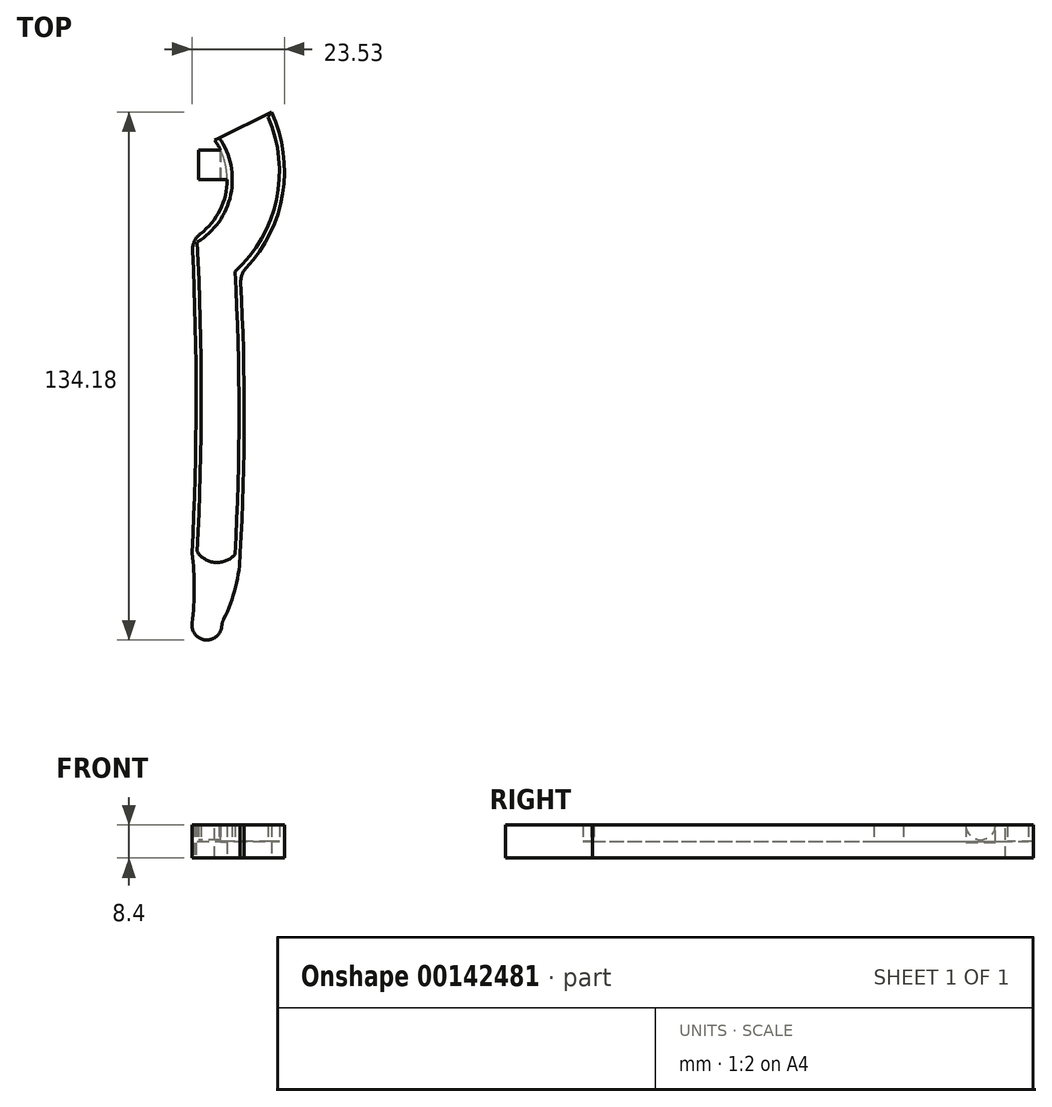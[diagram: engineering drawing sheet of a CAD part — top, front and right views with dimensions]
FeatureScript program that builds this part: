
annotation { "Feature Type Name" : "Feature", "Feature Type Description" : "" }
export const myFeature = defineFeature(function(context is Context, id is Id, definition is map)
    precondition{}
    {
        {
            var Q0;
            Q0=qCreatedBy(makeId("Top.planeOp"),FACE);
            var sketch = newSketch(context, id + "F0", { "sketchPlane" : qUnion([Q0])});
            skArc(sketch, "E0", {"start": v(-18, -31.8) * mm, "mid": v(-9.08, -15.9) * mm, "end": v(-18, 0) * mm});
            skArc(sketch, "E1", {"start": v(-8.38, -39.3) * mm, "mid": v(2.12, -21) * mm, "end": v(0, 0) * mm});
            skArc(sketch, "E2", {"start": v(-18, -110.4) * mm, "mid": v(-17, -71.1) * mm, "end": v(-18, -31.8) * mm});
            skArc(sketch, "E3", {"start": v(-8.38, -111.1) * mm, "mid": v(-7.37, -75.2) * mm, "end": v(-8.38, -39.3) * mm});
            skArc(sketch, "E4", {"start": v(-18, -110.4) * mm, "mid": v(-13.37, -113.18) * mm, "end": v(-8.38, -111.1) * mm});
            skLineSegment(sketch, "E5", {"start": v(0, 0) * mm, "end": v(-18, 0) * mm});
            skArc(sketch, "E6.0", {"start": v(-19.32, -110.8) * mm, "mid": v(-18.3, -70.94) * mm, "end": v(-19.34, -31.07) * mm});
            skLineSegment(sketch, "E6.1", {"start": v(0.84, 1.3) * mm, "end": v(-25.59, 1.3) * mm});
            skArc(sketch, "E6.2", {"start": v(-7.05, -39.84) * mm, "mid": v(3.54, -20.54) * mm, "end": v(0.84, 1.3) * mm});
            skArc(sketch, "E6.3", {"start": v(-19.34, -31.07) * mm, "mid": v(-10.7, -12.62) * mm, "end": v(-25.59, 1.3) * mm});
            skArc(sketch, "E6.4", {"start": v(-7.06, -110.8) * mm, "mid": v(-6.07, -75.32) * mm, "end": v(-7.05, -39.84) * mm});
            skArc(sketch, "E7", {"start": v(-19.32, -128.6) * mm, "mid": v(-18.75, -119.7) * mm, "end": v(-19.32, -110.8) * mm});
            skArc(sketch, "E8", {"start": v(-11.78, -128.6) * mm, "mid": v(-8.38, -119.98) * mm, "end": v(-7.06, -110.8) * mm});
            skArc(sketch, "E9", {"start": v(-19.32, -128.6) * mm, "mid": v(-15.55, -132.88) * mm, "end": v(-11.78, -128.6) * mm});
            skArc(sketch, "E10", {"start": v(-18.93, -124.62) * mm, "mid": v(-23.1, -126.21) * mm, "end": v(-19.32, -128.6) * mm});
            skCircle(sketch, "E11", {"center": v(-20.62, -126.46) * mm, "radius": 1 * mm});
            skLineSegment(sketch, "E12", {"start": v(-10.38, -15.9) * mm, "end": v(-17.68, -15.9) * mm});
            skLineSegment(sketch, "E13", {"start": v(-17.68, -15.9) * mm, "end": v(-17.68, -8.4) * mm});
            skLineSegment(sketch, "E14", {"start": v(-17.68, -8.4) * mm, "end": v(-12.09, -8.4) * mm});
            skSolve(sketch);
        }
        {
            var Q0;
            Q0=makeQuery(id+"F0.imprint","IMPRINT",FACE,{"disambiguationData":[TD([[makeQuery(id+"F0.imprint","IMPRINT",EDGE,{"derivedFrom":sQuery(id+"F0.wireOp",EDGE,"E0")}),1.0]])]});
            extrude(context, id + "F1", {"entities" : qUnion([Q0]), "depth" : 8.4 * mm});
        }
        {
            var Q0;
            Q0=makeQuery(id+"F0.imprint","IMPRINT",FACE,{"disambiguationData":[TD([[makeQuery(id+"F0.imprint","IMPRINT",EDGE,{"derivedFrom":sQuery(id+"F0.wireOp",EDGE,"E0")}),-1.0]])]});
            extrude(context, id + "F2", {"entities" : qUnion([Q0]), "operationType" : NewBodyOperationType.ADD, "depth" : 4.2 * mm});
        }
        {
            var Q0;
            {var subQ0=sQuery(id+"F0.wireOp",EDGE,"E12");Q0=makeQuery(id+"F0.imprint","IMPRINT",FACE,{"disambiguationData":[TD([[makeQuery(id+"F0.imprint","IMPRINT",EDGE,{"derivedFrom":subQ0}),-1.0]])]});}
            extrude(context, id + "F3", {"entities" : qUnion([Q0]), "operationType" : NewBodyOperationType.ADD, "depth" : 8.4 * mm});
        }
        {
            var Q0;
            {var subQ0=sQuery(id+"F0.wireOp",EDGE,"E12");Q0=makeQuery(id+"F0.imprint","IMPRINT",FACE,{"disambiguationData":[TD([[makeQuery(id+"F0.imprint","IMPRINT",EDGE,{"derivedFrom":subQ0}),-1.0]])]});}
            extrude(context, id + "F4", {"entities" : qUnion([Q0]), "operationType" : NewBodyOperationType.REMOVE, "depth" : 4 * mm});
        }
        {
            var Q0;
            Q0=makeQuery(id+"F3.opExtrude","SWEPT_FACE",FACE,{"disambiguationData":[OSD([sQuery(id+"F0.wireOp",EDGE,"E13")])]});
            var sketch = newSketch(context, id + "F5", { "sketchPlane" : qUnion([Q0])});
            skLineSegment(sketch, "E15.0", {"start": v(8.4, 8.4) * mm, "end": v(8.4, 4) * mm});
            skLineSegment(sketch, "E15.1", {"start": v(15.9, 8.4) * mm, "end": v(8.4, 8.4) * mm});
            skLineSegment(sketch, "E15.2", {"start": v(15.9, 8.4) * mm, "end": v(15.9, 4) * mm});
            skLineSegment(sketch, "E15.3", {"start": v(15.9, 4) * mm, "end": v(8.4, 4) * mm});
            skSolve(sketch);
        }
        {
            var Q0;
            {var subQ0=sQuery(id+"F0.wireOp",EDGE,"E6.3");Q0=makeQuery(id+"F3.boolean.opBoolean","MERGE",FACE,{"derivedFrom":[makeQuery(id+"F1.opExtrude","CAP_FACE",FACE,{"disambiguationData":[OSD([sQuery(id+"F0.wireOp",EDGE,"E0"),sQuery(id+"F0.wireOp",EDGE,"E1"),sQuery(id+"F0.wireOp",EDGE,"E2"),sQuery(id+"F0.wireOp",EDGE,"E3"),sQuery(id+"F0.wireOp",EDGE,"E4"),sQuery(id+"F0.wireOp",EDGE,"E5"),sQuery(id+"F0.wireOp",EDGE,"E6.0"),sQuery(id+"F0.wireOp",EDGE,"E6.1"),sQuery(id+"F0.wireOp",EDGE,"E6.2"),subQ0,sQuery(id+"F0.wireOp",EDGE,"E6.4"),sQuery(id+"F0.wireOp",EDGE,"E7"),sQuery(id+"F0.wireOp",EDGE,"E8"),sQuery(id+"F0.wireOp",EDGE,"E9"),sQuery(id+"F0.wireOp",EDGE,"E10"),sQuery(id+"F0.wireOp",EDGE,"E11")])],"isStart":false}),makeQuery(id+"F3.opExtrude","CAP_FACE",FACE,{"disambiguationData":[OSD([subQ0,sQuery(id+"F0.wireOp",EDGE,"E12"),sQuery(id+"F0.wireOp",EDGE,"E13"),sQuery(id+"F0.wireOp",EDGE,"E14")])],"isStart":false})]});}
            var sketch = newSketch(context, id + "F6", { "sketchPlane" : qUnion([Q0])});
            skLineSegment(sketch, "E16.0", {"start": v(0.84, 1.3) * mm, "end": v(-25.59, 1.3) * mm});
            skArc(sketch, "E16.1", {"start": v(-7.05, -39.84) * mm, "mid": v(3.54, -20.54) * mm, "end": v(0.84, 1.3) * mm});
            skArc(sketch, "E16.2", {"start": v(-12.09, -8.4) * mm, "mid": v(-17.6, -1.83) * mm, "end": v(-25.59, 1.3) * mm});
            skLineSegment(sketch, "E16.3", {"start": v(-17.68, -8.4) * mm, "end": v(-12.09, -8.4) * mm});
            skLineSegment(sketch, "E17", {"start": v(0.84, 1.3) * mm, "end": v(-13.56, -5.9) * mm});
            skSolve(sketch);
        }
        {
            var Q0;
            {var subQ1=sQuery(id+"F6.wireOp",EDGE,"E16.0");Q0=makeQuery(id+"F6.imprint","IMPRINT",FACE,{"disambiguationData":[TD([[makeQuery(id+"F6.imprint","IMPRINT",EDGE,{"derivedFrom":subQ1}),1.0]])]});}
            var Q1;
            {var subQ0=sQuery(id+"F6.wireOp",EDGE,"E17");var subQ1=makeQuery(id+"F1.opExtrude","CAP_EDGE",EDGE,{"disambiguationData":[OSD([sQuery(id+"F0.wireOp",EDGE,"E5")])],"isStart":false});var subQ2=makeQuery(id+"F6.imprint","INTERSECT",VERTEX,{"derivedFrom":[subQ1,subQ0]});Q1=makeQuery(id+"F6.imprint","IMPRINT",FACE,{"disambiguationData":[TD([[makeQuery(id+"F6.imprint","IMPRINT",EDGE,{"disambiguationData":[TD([[subQ2,-1.0]])],"derivedFrom":subQ0}),-1.0]])]});}
            extrude(context, id + "F7", {"entities" : qUnion([Q0, Q1]), "operationType" : NewBodyOperationType.REMOVE, "oppositeDirection" : true, "depth" : 25 * mm});
        }
        {
            var Q0;
            {var subQ0=sQuery(id+"F0.wireOp",EDGE,"E6.3");Q0=makeQuery(id+"F3.boolean.opBoolean","MERGE",FACE,{"derivedFrom":[makeQuery(id+"F1.opExtrude","CAP_FACE",FACE,{"disambiguationData":[OSD([sQuery(id+"F0.wireOp",EDGE,"E0"),sQuery(id+"F0.wireOp",EDGE,"E1"),sQuery(id+"F0.wireOp",EDGE,"E2"),sQuery(id+"F0.wireOp",EDGE,"E3"),sQuery(id+"F0.wireOp",EDGE,"E4"),sQuery(id+"F0.wireOp",EDGE,"E5"),sQuery(id+"F0.wireOp",EDGE,"E6.0"),sQuery(id+"F0.wireOp",EDGE,"E6.1"),sQuery(id+"F0.wireOp",EDGE,"E6.2"),subQ0,sQuery(id+"F0.wireOp",EDGE,"E6.4"),sQuery(id+"F0.wireOp",EDGE,"E7"),sQuery(id+"F0.wireOp",EDGE,"E8"),sQuery(id+"F0.wireOp",EDGE,"E9"),sQuery(id+"F0.wireOp",EDGE,"E10"),sQuery(id+"F0.wireOp",EDGE,"E11")])],"isStart":false}),makeQuery(id+"F3.opExtrude","CAP_FACE",FACE,{"disambiguationData":[OSD([subQ0,sQuery(id+"F0.wireOp",EDGE,"E12"),sQuery(id+"F0.wireOp",EDGE,"E13"),sQuery(id+"F0.wireOp",EDGE,"E14")])],"isStart":false})]});}
            var sketch = newSketch(context, id + "F8", { "sketchPlane" : qUnion([Q0])});
            skArc(sketch, "E18.0", {"start": v(-7.05, -39.84) * mm, "mid": v(3.54, -20.54) * mm, "end": v(0.84, 1.3) * mm});
            skLineSegment(sketch, "E18.1", {"start": v(0.84, 1.3) * mm, "end": v(-1.76, 0) * mm});
            skLineSegment(sketch, "E18.2", {"start": v(0, 0) * mm, "end": v(-1.76, 0) * mm});
            skArc(sketch, "E18.3", {"start": v(-8.38, -39.3) * mm, "mid": v(2.12, -21) * mm, "end": v(0, 0) * mm});
            skLineSegment(sketch, "E19", {"start": v(0.84, 1.3) * mm, "end": v(0, 0) * mm});
            skSolve(sketch);
        }
        {
            var Q0;
            Q0=makeQuery(id+"F8.imprint","IMPRINT",FACE,{"disambiguationData":[TD([[makeQuery(id+"F8.imprint","IMPRINT",EDGE,{"derivedFrom":sQuery(id+"F8.wireOp",EDGE,"E18.1")}),1.0]])]});
            extrude(context, id + "F9", {"entities" : qUnion([Q0]), "operationType" : NewBodyOperationType.REMOVE, "oppositeDirection" : true, "depth" : 4.2 * mm});
        }
        {
            var Q0;
            Q0=makeQuery(id+"F5.imprint","IMPRINT",FACE,{"disambiguationData":[TD([[makeQuery(id+"F5.imprint","IMPRINT",EDGE,{"derivedFrom":sQuery(id+"F5.wireOp",EDGE,"E15.0")}),1.0]])]});
            var sketch = newSketch(context, id + "F10", { "sketchPlane" : qUnion([Q0])});
            skLineSegment(sketch, "E20.0", {"start": v(15.9, 8.4) * mm, "end": v(8.4, 8.4) * mm});
            skLineSegment(sketch, "E20.1", {"start": v(8.4, 8.4) * mm, "end": v(8.4, 4) * mm});
            skLineSegment(sketch, "E20.2", {"start": v(15.9, 4) * mm, "end": v(8.4, 4) * mm});
            skLineSegment(sketch, "E20.3", {"start": v(15.9, 8.4) * mm, "end": v(15.9, 4) * mm});
            skArc(sketch, "E21", {"start": v(8.4, 8.4) * mm, "mid": v(12.15, 4.65) * mm, "end": v(15.9, 8.4) * mm});
            skSolve(sketch);
        }
        {
            var Q0;
            Q0=makeQuery(id+"F10.imprint","IMPRINT",FACE,{"disambiguationData":[TD([[makeQuery(id+"F10.imprint","IMPRINT",EDGE,{"derivedFrom":sQuery(id+"F10.wireOp",EDGE,"E20.2")}),-1.0]])]});
            extrude(context, id + "F11", {"entities" : qUnion([Q0]), "operationType" : NewBodyOperationType.REMOVE, "oppositeDirection" : true, "depth" : 5.6 * mm});
        }
        {
            var Q0;
            Q0=makeQuery(id+"F1.opExtrude","SWEPT_EDGE",EDGE,{"disambiguationData":[OSD([sQuery(id+"F0.wireOp",EDGE,"E6.2"),sQuery(id+"F0.wireOp",EDGE,"E6.4")])]});
            var Q1;
            Q1=makeQuery(id+"F1.opExtrude","SWEPT_EDGE",EDGE,{"disambiguationData":[OSD([sQuery(id+"F0.wireOp",EDGE,"E6.0"),sQuery(id+"F0.wireOp",EDGE,"E6.3")])]});
            var Q2;
            Q2=makeQuery(id+"F1.opExtrude","SWEPT_EDGE",EDGE,{"disambiguationData":[OSD([sQuery(id+"F0.wireOp",EDGE,"E8"),sQuery(id+"F0.wireOp",EDGE,"E9")])]});
            fillet(context, id + "F12", {"entities" : qUnion([Q0, Q1, Q2]), "radius" : 5 * mm, "tangentPropagation" : true, "allowEdgeOverflow" : false});
        }
    });
